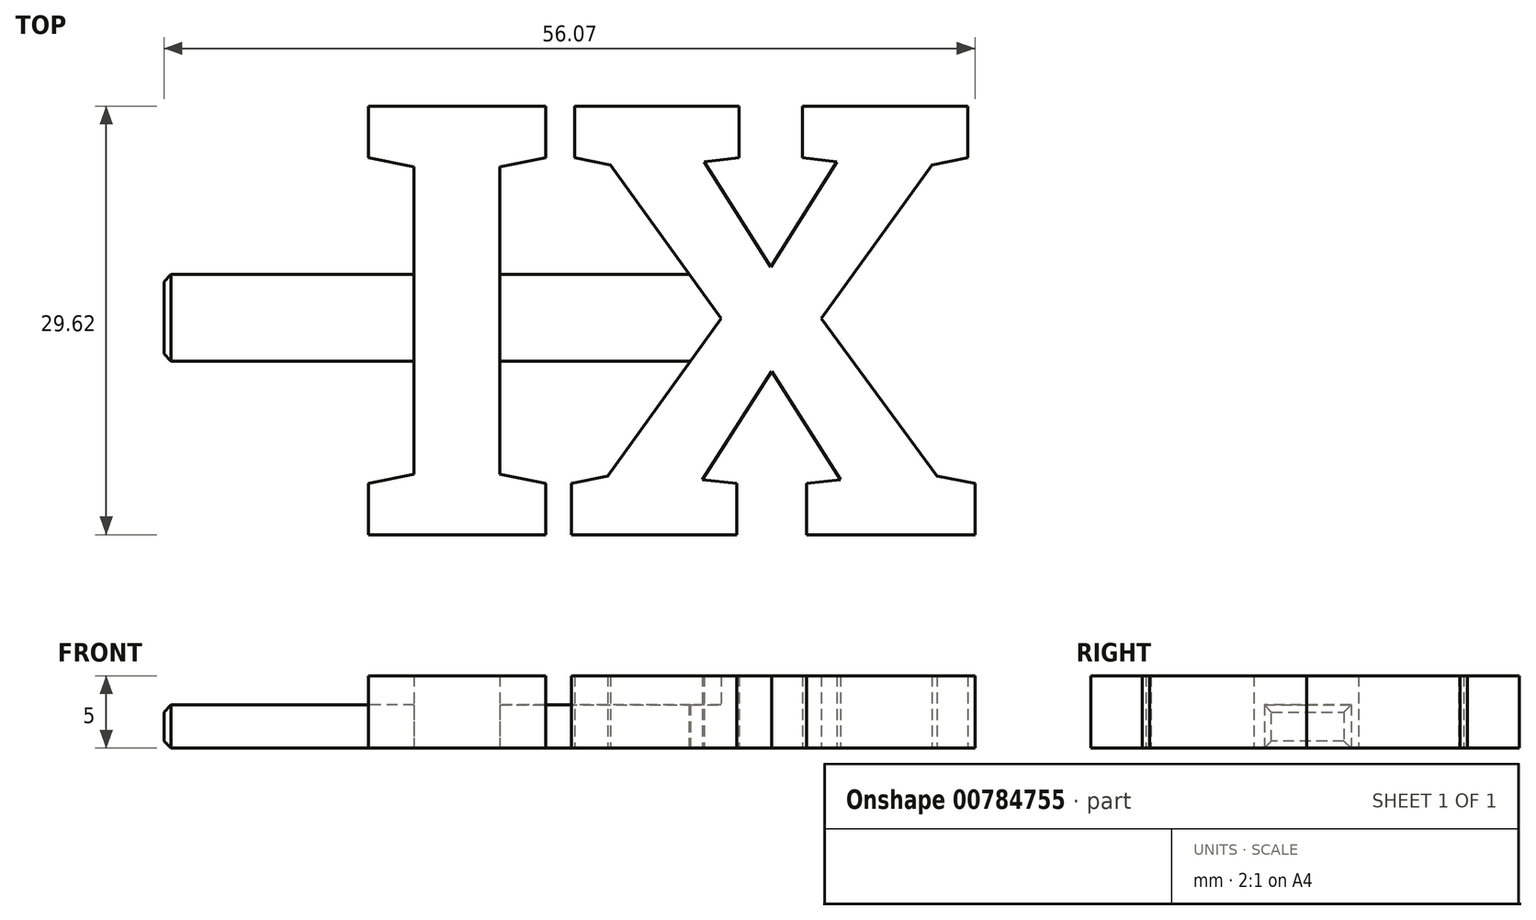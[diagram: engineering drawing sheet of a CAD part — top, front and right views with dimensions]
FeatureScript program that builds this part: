
annotation { "Feature Type Name" : "Feature", "Feature Type Description" : "" }
export const myFeature = defineFeature(function(context is Context, id is Id, definition is map)
    precondition{}
    {
        {
            var Q0;
            Q0=qCreatedBy(makeId("Top.planeOp"),FACE);
            var sketch = newSketch(context, id + "F0", { "sketchPlane" : qUnion([Q0])});
            skLineSegment(sketch, "E0.bottom", {"start": v(-14.7, 15) * mm, "end": v(14.7, 15) * mm, "construction": true});
            skText(sketch, "E1", { "text": "IX", "fontName": "RobotoSlab-Bold.ttf"});
            skLineSegment(sketch, "E2.bottom", {"start": v(-12.5, 3) * mm, "end": v(12.5, 3) * mm});
            skLineSegment(sketch, "E2.top", {"start": v(-12.5, -3) * mm, "end": v(12.5, -3) * mm});
            skLineSegment(sketch, "E3.bottom", {"start": v(-12.5, 3) * mm, "end": v(-35.81, 3) * mm});
            skLineSegment(sketch, "E3.top", {"start": v(-12.5, -3) * mm, "end": v(-35.81, -3) * mm});
            skLineSegment(sketch, "E3.right", {"start": v(-35.81, 3) * mm, "end": v(-35.81, -3) * mm});
            const initialGuessF0  = {"E1": [-0.02281, -0.015, 1, 0, 0.03]};
            skSetInitialGuess(sketch, initialGuessF0);
            skSolve(sketch);
        }
        {
            var Q0;
            Q0=makeQuery(id+"F0.imprint","IMPRINT",FACE,{"disambiguationData":[TD([[makeQuery(id+"F0.imprint","IMPRINT",EDGE,{"derivedFrom":sQuery(id+"F0.wireOp",EDGE,"E1.sketch_text.stroke-0")}),-1.0]])]});
            var Q1;
            {var subQ0=sQuery(id+"F0.wireOp",EDGE,"E3.bottom");var subQ1=sQuery(id+"F0.wireOp",EDGE,"E1.sketch_text.stroke-4");var subQ2=makeQuery(id+"F0.imprint","INTERSECT",VERTEX,{"derivedFrom":[subQ1,subQ0]});Q1=makeQuery(id+"F0.imprint","IMPRINT",FACE,{"disambiguationData":[TD([[makeQuery(id+"F0.imprint","IMPRINT",EDGE,{"disambiguationData":[TD([[subQ2,-1.0]])],"derivedFrom":subQ1}),-1.0]])]});}
            var Q2;
            {var subQ0=sQuery(id+"F0.wireOp",EDGE,"E1.sketch_text.stroke-5");Q2=makeQuery(id+"F0.imprint","IMPRINT",FACE,{"disambiguationData":[TD([[makeQuery(id+"F0.imprint","IMPRINT",EDGE,{"derivedFrom":subQ0}),-1.0]])]});}
            var Q3;
            {var subQ1=sQuery(id+"F0.wireOp",EDGE,"E1.sketch_text.stroke-12");Q3=makeQuery(id+"F0.imprint","IMPRINT",FACE,{"disambiguationData":[TD([[makeQuery(id+"F0.imprint","IMPRINT",EDGE,{"derivedFrom":subQ1}),-1.0]])]});}
            var Q4;
            {var subQ7=sQuery(id+"F0.wireOp",EDGE,"E1.sketch_text.stroke-14");var subQ8=sQuery(id+"F0.wireOp",EDGE,"E1.sketch_text.stroke-13");var subQ9=makeQuery(id+"F0.imprint","INTERSECT",VERTEX,{"derivedFrom":[subQ8,subQ7]});Q4=makeQuery(id+"F0.imprint","IMPRINT",FACE,{"disambiguationData":[TD([[makeQuery(id+"F0.imprint","IMPRINT",EDGE,{"disambiguationData":[TD([[subQ9,1.0]])],"derivedFrom":subQ8}),-1.0]])]});}
            var Q5;
            {var subQ5=sQuery(id+"F0.wireOp",EDGE,"E1.sketch_text.stroke-15");Q5=makeQuery(id+"F0.imprint","IMPRINT",FACE,{"disambiguationData":[TD([[makeQuery(id+"F0.imprint","IMPRINT",EDGE,{"derivedFrom":subQ5}),-1.0]])]});}
            extrude(context, id + "F1", {"entities" : qUnion([Q0, Q1, Q2, Q3, Q4, Q5]), "depth" : 5 * mm, "offsetDistance" : 25 * mm});
        }
        {
            var Q0;
            {var subQ5=sQuery(id+"F0.wireOp",EDGE,"E3.bottom");var subQ7=sQuery(id+"F0.wireOp",EDGE,"E1.sketch_text.stroke-4");var subQ8=makeQuery(id+"F0.imprint","INTERSECT",VERTEX,{"derivedFrom":[subQ7,subQ5]});Q0=makeQuery(id+"F0.imprint","IMPRINT",FACE,{"disambiguationData":[TD([[makeQuery(id+"F0.imprint","IMPRINT",EDGE,{"disambiguationData":[TD([[subQ8,-1.0]])],"derivedFrom":subQ7}),1.0]])]});}
            var Q1;
            {var subQ5=sQuery(id+"F0.wireOp",EDGE,"E3.right");Q1=makeQuery(id+"F0.imprint","IMPRINT",FACE,{"disambiguationData":[TD([[makeQuery(id+"F0.imprint","IMPRINT",EDGE,{"derivedFrom":subQ5}),1.0]])]});}
            extrude(context, id + "F2", {"entities" : qUnion([Q0, Q1]), "operationType" : NewBodyOperationType.ADD, "depth" : 3 * mm, "offsetDistance" : 25 * mm});
        }
        {
            var Q0;
            Q0=makeQuery(id+"F2.opExtrude","CAP_EDGE",EDGE,{"disambiguationData":[OSD([sQuery(id+"F0.wireOp",EDGE,"E3.right")])],"isStart":true});
            var Q1;
            Q1=makeQuery(id+"F2.opExtrude","SWEPT_EDGE",EDGE,{"disambiguationData":[OSD([sQuery(id+"F0.wireOp",EDGE,"E3.bottom"),sQuery(id+"F0.wireOp",EDGE,"E3.right")])]});
            var Q2;
            Q2=makeQuery(id+"F2.opExtrude","CAP_EDGE",EDGE,{"disambiguationData":[OSD([sQuery(id+"F0.wireOp",EDGE,"E3.right")])],"isStart":false});
            var Q3;
            Q3=makeQuery(id+"F2.opExtrude","SWEPT_EDGE",EDGE,{"disambiguationData":[OSD([sQuery(id+"F0.wireOp",EDGE,"E3.top"),sQuery(id+"F0.wireOp",EDGE,"E3.right")])]});
            chamfer(context, id + "F3", {"entities" : qUnion([Q0, Q1, Q2, Q3]), "width" : 0.5 * mm, "tangentPropagation" : true});
        }
    });
